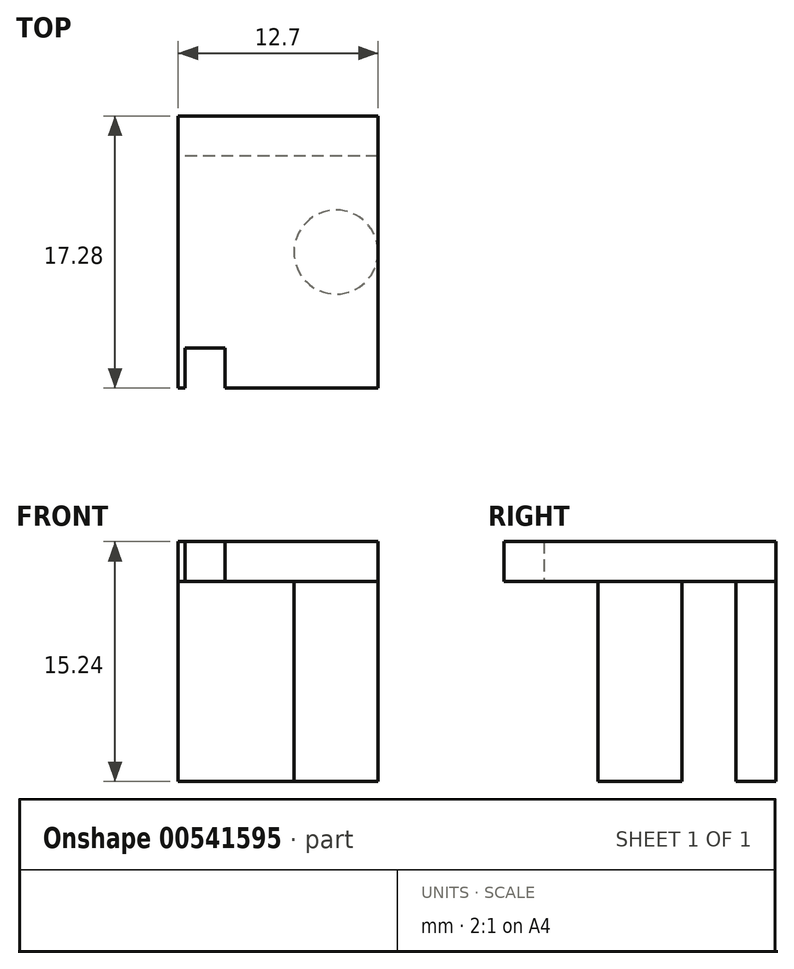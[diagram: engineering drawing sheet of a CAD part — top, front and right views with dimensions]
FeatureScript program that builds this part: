
annotation { "Feature Type Name" : "Feature", "Feature Type Description" : "" }
export const myFeature = defineFeature(function(context is Context, id is Id, definition is map)
    precondition{}
    {
        {
            var Q0;
            Q0=qCreatedBy(makeId("Top.planeOp"),FACE);
            var sketch = newSketch(context, id + "F0", { "sketchPlane" : qUnion([Q0])});
            skCircle(sketch, "E0", {"center": v(0, 0) * mm, "radius": 2.8 * mm, "construction": true});
            skLineSegment(sketch, "E1", {"start": v(-17.94, 0) * mm, "end": v(20.34, 0) * mm, "construction": true});
            skCircle(sketch, "E2", {"center": v(0, 0) * mm, "radius": 2.67 * mm});
            skLineSegment(sketch, "E3.bottom", {"start": v(2.67, 8.64) * mm, "end": v(-10.03, 8.64) * mm});
            skLineSegment(sketch, "E3.top", {"start": v(2.67, 6.1) * mm, "end": v(-10.03, 6.1) * mm});
            skLineSegment(sketch, "E3.left", {"start": v(2.67, 8.64) * mm, "end": v(2.67, 6.1) * mm});
            skLineSegment(sketch, "E3.right", {"start": v(-10.03, 8.64) * mm, "end": v(-10.03, 6.1) * mm});
            skPoint(sketch, "E3.middle", {"position": v(0, 7.37) * mm});
            skSolve(sketch);
        }
        {
            var Q0;
            Q0 = qSketchRegion(id + "F0", true);
            extrude(context, id + "F1", {"entities" : qUnion([Q0]), "oppositeDirection" : true, "depth" : 12.7 * mm, "offsetDistance" : 25.4 * mm});
        }
        {
            var Q0;
            Q0=qCreatedBy(makeId("Top.planeOp"),FACE);
            var sketch = newSketch(context, id + "F2", { "sketchPlane" : qUnion([Q0])});
            skLineSegment(sketch, "E4.bottom", {"start": v(2.67, 8.64) * mm, "end": v(-10.03, 8.64) * mm});
            skLineSegment(sketch, "E4.top", {"start": v(2.67, -8.64) * mm, "end": v(-7.04, -8.64) * mm});
            skLineSegment(sketch, "E4.left", {"start": v(2.67, 8.64) * mm, "end": v(2.67, -8.64) * mm});
            skLineSegment(sketch, "E4.right", {"start": v(-10.03, 8.64) * mm, "end": v(-10.03, -8.64) * mm});
            skPoint(sketch, "E4.middle", {"position": v(-3.68, 0) * mm});
            skLineSegment(sketch, "E5", {"start": v(-10.03, -8.64) * mm, "end": v(-9.58, -8.64) * mm});
            skLineSegment(sketch, "E6", {"start": v(-9.58, -8.64) * mm, "end": v(-9.58, -6.1) * mm});
            skLineSegment(sketch, "E7", {"start": v(-9.58, -6.1) * mm, "end": v(-7.04, -6.1) * mm});
            skLineSegment(sketch, "E8", {"start": v(-7.04, -6.1) * mm, "end": v(-7.04, -8.64) * mm});
            skSolve(sketch);
        }
        {
            var Q0;
            Q0 = qSketchRegion(id + "F2", true);
            extrude(context, id + "F3", {"entities" : qUnion([Q0]), "depth" : 2.54 * mm, "offsetDistance" : 25.4 * mm});
        }
    });
